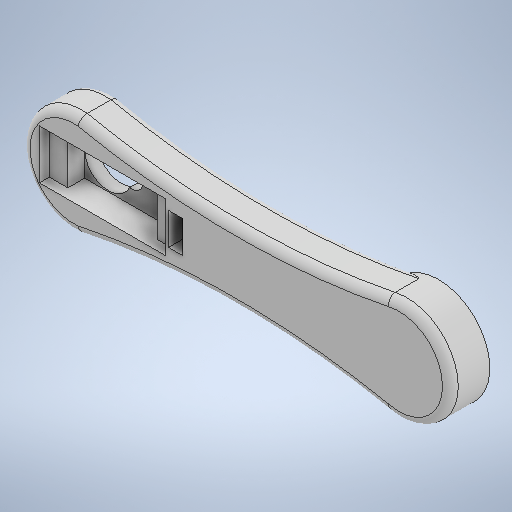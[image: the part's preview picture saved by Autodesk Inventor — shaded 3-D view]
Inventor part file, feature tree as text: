
AUTODESK INVENTOR PART (.ipt)
format: ipt  version: 2025.2 (Build 292293000, 293)  size: 769,536 bytes
history: native  units: mm
features: sketch x10, extrude x10, other x1, fillet x1
ambient origin geometry x8: Origin, YZ Plane, XZ Plane, XY Plane, X Axis, Y Axis, Z Axis, Center Point
bodies: Body1 (feature_tree)
feature tree (22):
  other  "Bryła1"
  sketch  "Szkic1"
  extrude  "Wyciągnięcie proste1"  Depth=13.0mm
  extrude  "Wyciągnięcie proste3"  Depth=10.0mm TaperAngle=0.0deg
  extrude  "Wyciągnięcie proste4"  Depth=32.0mm
  extrude  "Wyciągnięcie proste5"  Depth=12.5mm
  sketch  "Szkic5"
  extrude  "Wyciągnięcie proste6"  Depth=2.5mm TaperAngle=0.0deg
  extrude  "Wyciągnięcie proste7"  Depth=22.6mm
  fillet  "Zaokrąglenie1"  Radius=4.25mm
  sketch  "Szkic6"
  extrude  "Wyciągnięcie proste10"  Depth=12.0mm
  extrude  "Wyciągnięcie proste11"  Depth=5.4mm
  extrude  "Wyciągnięcie proste12"  Depth=4.25mm TaperAngle=0.0deg
  extrude  "Wyciągnięcie proste13"  Depth=10.0mm TaperAngle=0.0deg
  sketch  "Szkic2"
  sketch  "Szkic3"
  sketch  "Szkic4"
  sketch  "Szkic7"
  sketch  "Szkic8"
  sketch  "Szkic9"
  sketch  "Szkic10"
